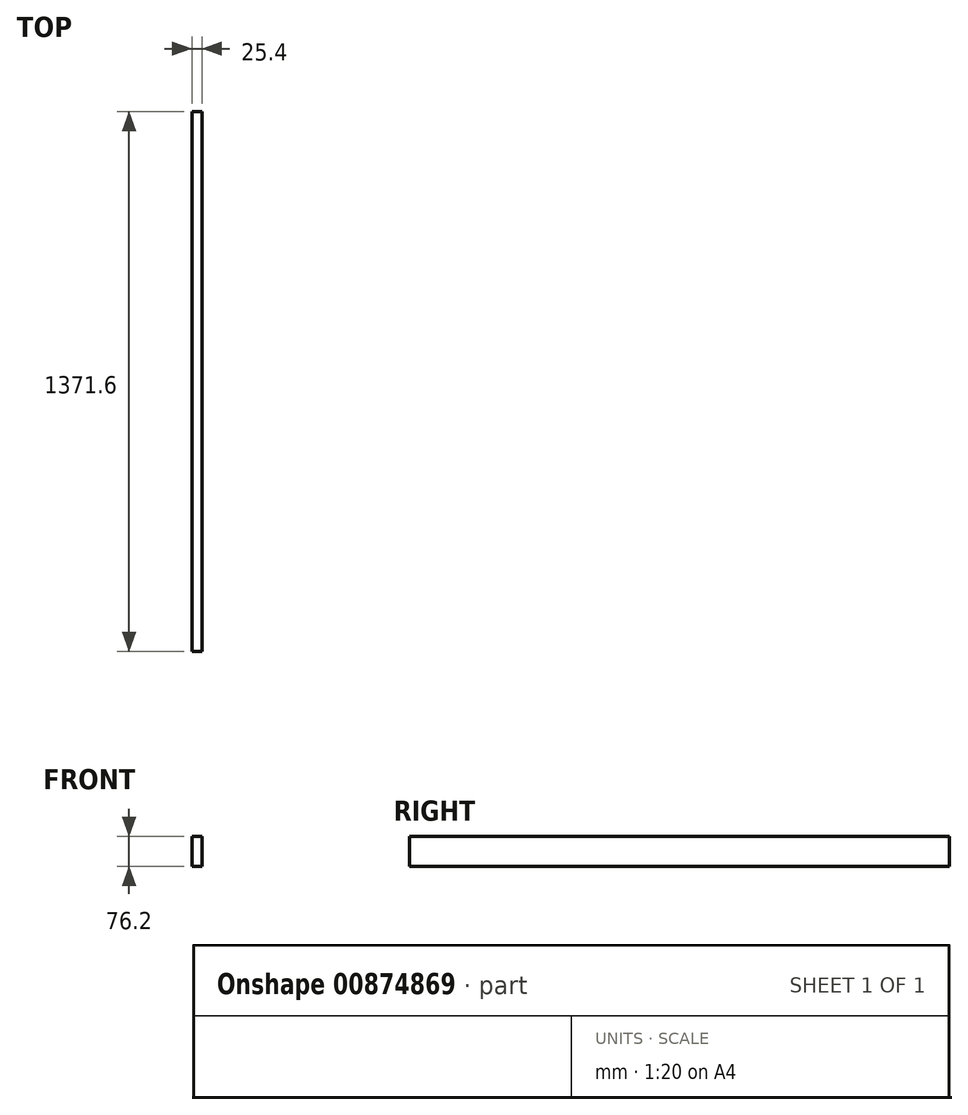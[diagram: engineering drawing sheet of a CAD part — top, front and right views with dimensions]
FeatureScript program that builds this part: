
annotation { "Feature Type Name" : "Feature", "Feature Type Description" : "" }
export const myFeature = defineFeature(function(context is Context, id is Id, definition is map)
    precondition{}
    {
        {
            var Q0;
            Q0=qCreatedBy(makeId("Front.planeOp"),FACE);
            var sketch = newSketch(context, id + "F0", { "sketchPlane" : qUnion([Q0])});
            skLineSegment(sketch, "E0", {"start": v(-41.66, 35.4) * mm, "end": v(-16.26, 35.4) * mm});
            skLineSegment(sketch, "E1", {"start": v(-16.26, 35.4) * mm, "end": v(-16.26, -40.8) * mm});
            skLineSegment(sketch, "E2", {"start": v(-16.26, -40.8) * mm, "end": v(-41.66, -40.8) * mm});
            skLineSegment(sketch, "E3", {"start": v(-41.66, -40.8) * mm, "end": v(-41.66, 35.4) * mm});
            skSolve(sketch);
        }
        {
            var Q0;
            Q0 = qSketchRegion(id + "F0", true);
            extrude(context, id + "F1", {"entities" : qUnion([Q0]), "depth" : 1371.6 * mm, "offsetDistance" : 25.4 * mm});
        }
    });
